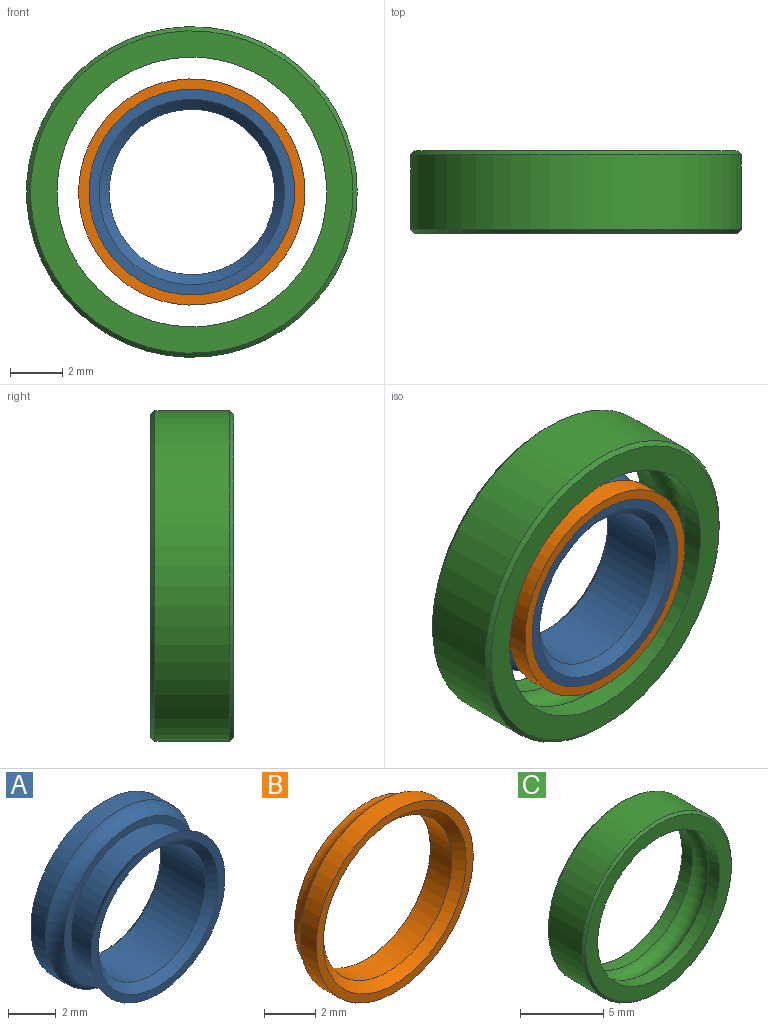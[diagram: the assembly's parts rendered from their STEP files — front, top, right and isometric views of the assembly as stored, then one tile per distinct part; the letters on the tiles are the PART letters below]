
ASSEMBLY  parts=3 mates=2
PART A: 10 faces, bbox 10.3x3.2x10.3 mm
  f0: plane 7.9x7.9mm, normal (0,-1,0), area 9.3mm2, adj f1,f9
  f1: cone r=3.56mm half-angle=45deg, axis (0,-1,0), area 13.1mm2, adj f0,f2
  f2: cylinder r=3.56mm len=7.12mm, axis (0,-1,0), area 26.7mm2, adj f1,f3
  f3: plane 7.88x7.88mm, normal (0,-1,0), area 9mm2, adj f2,f4
  f4: torus R=4.76mm, axis (0,-1,0), area 21.8mm2, adj f3,f5
  f5: cylinder r=4.34mm len=8.69mm, axis (0,-1,0), area 24.1mm2, adj f4,f6
  f6: plane 8.69x8.69mm, normal (0,1,0), area 24.4mm2, adj f5,f7
  f7: cone r=3.17mm half-angle=45deg, axis (0,1,0), area 4.6mm2, adj f6,f8
  f8: cylinder r=3.17mm len=6.35mm, axis (0,-1,0), area 52.5mm2, adj f7,f9
  f9: cone r=3.56mm half-angle=45deg, axis (0,-1,0), area 11.5mm2, adj f0,f8
PART B: 6 faces, bbox 10.3x1.6x10.3 mm
  f0: plane 8.69x8.69mm, normal (0,-1,0), area 10.2mm2, adj f1,f5
  f1: cone r=3.95mm half-angle=45deg, axis (0,-1,0), area 13.1mm2, adj f0,f2
  f2: cylinder r=3.56mm len=7.12mm, axis (0,-1,0), area 26.7mm2, adj f1,f3
  f3: plane 7.88x7.88mm, normal (0,1,0), area 9mm2, adj f2,f4
  f4: torus R=4.76mm, axis (0,-1,0), area 21.8mm2, adj f3,f5
  f5: cylinder r=4.34mm len=8.69mm, axis (0,-1,0), area 24.1mm2, adj f0,f4
PART C: 8 faces, bbox 12.7x3.2x12.7 mm
  f0: cone r=6.35mm half-angle=45deg, axis (0,1,0), area 8.8mm2, adj f1,f7
  f1: cylinder r=6.35mm len=12.7mm, axis (0,-1,0), area 114mm2, adj f0,f2
  f2: cone r=6.19mm half-angle=45deg, axis (0,-1,0), area 8.8mm2, adj f1,f3
  f3: plane 12.38x12.38mm, normal (0,1,0), area 36.1mm2, adj f2,f4
  f4: cylinder r=5.18mm len=10.36mm, axis (0,-1,0), area 28.7mm2, adj f3,f5
  f5: torus R=4.76mm, axis (0,-1,0), area 58.1mm2, adj f4,f6
  f6: cylinder r=5.18mm len=10.36mm, axis (0,-1,0), area 28.7mm2, adj f5,f7
  f7: plane 12.38x12.38mm, normal (0,-1,0), area 36.1mm2, adj f0,f6
PLACE A t=(0,0.01,0)mm
PLACE B t=(0,0.01,0)mm
PLACE C at identity
MATE fastened B.f1 <-> A.f1  axis (0,-1,0) through (0,-1.57,0)mm
MATE revolute A.f1 <-> C.f0  axis (0,-1,0) through (0,0.13,0)mm
